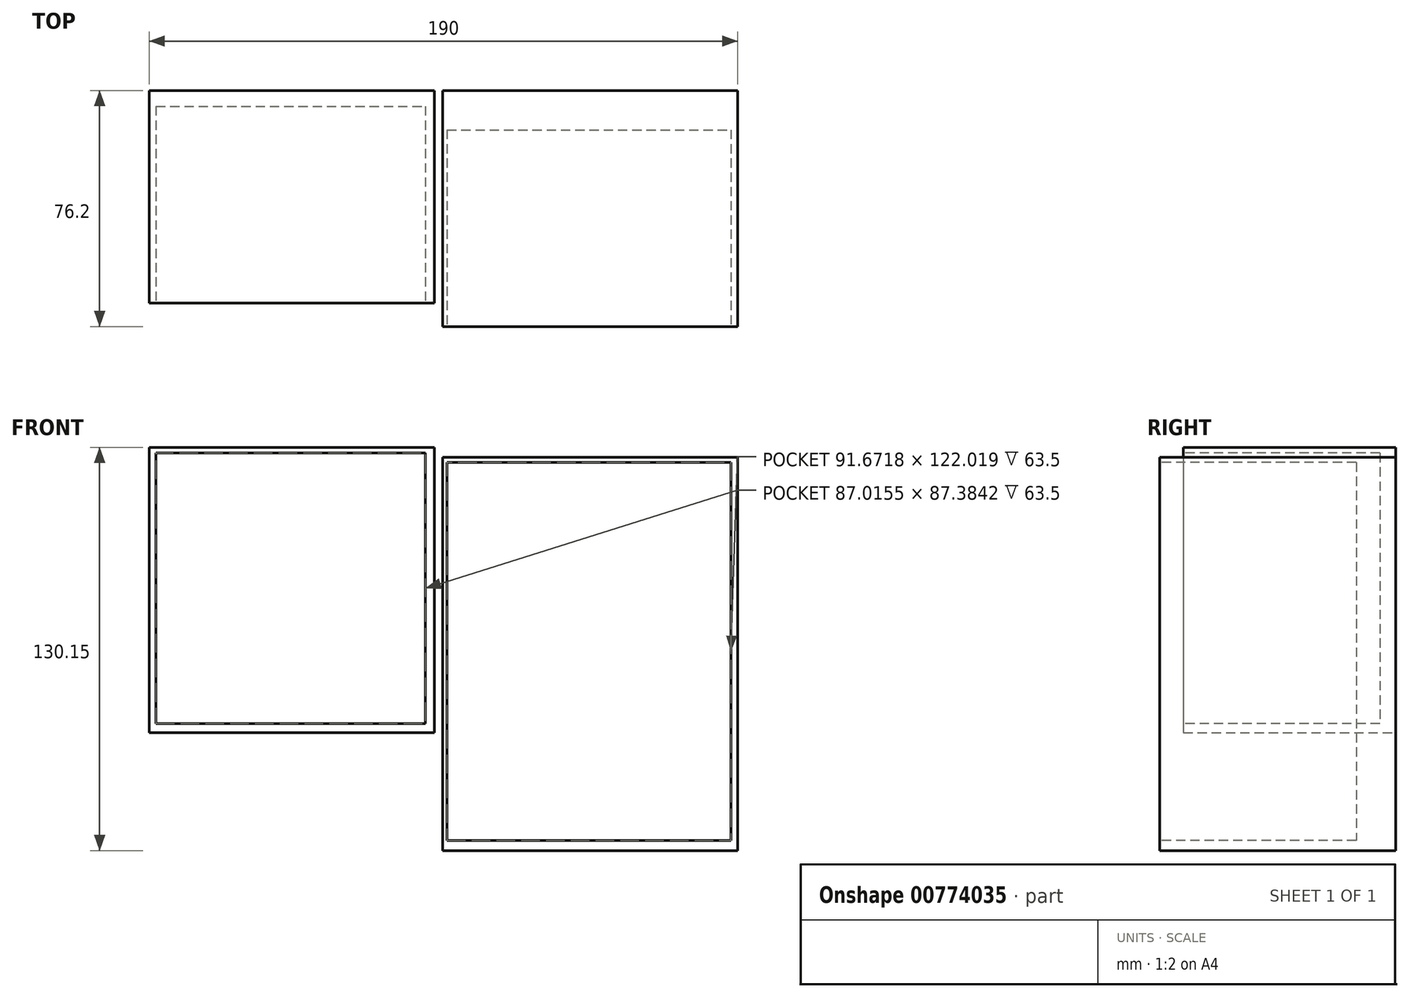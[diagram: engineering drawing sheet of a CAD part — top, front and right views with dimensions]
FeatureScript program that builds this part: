
annotation { "Feature Type Name" : "Feature", "Feature Type Description" : "" }
export const myFeature = defineFeature(function(context is Context, id is Id, definition is map)
    precondition{}
    {
        {
            var Q0;
            Q0=qCreatedBy(makeId("Front.planeOp"),FACE);
            var sketch = newSketch(context, id + "F0", { "sketchPlane" : qUnion([Q0])});
            skLineSegment(sketch, "E0.bottom", {"start": v(-81.71, 66.08) * mm, "end": v(10.36, 66.08) * mm});
            skLineSegment(sketch, "E0.top", {"start": v(-81.71, -26) * mm, "end": v(10.36, -26) * mm});
            skLineSegment(sketch, "E0.left", {"start": v(-81.71, 66.08) * mm, "end": v(-81.71, -26) * mm});
            skLineSegment(sketch, "E0.right", {"start": v(10.36, 66.08) * mm, "end": v(10.36, -26) * mm});
            skSolve(sketch);
        }
        {
            var Q0;
            Q0=makeQuery(id+"F0.imprint","IMPRINT",FACE,{"disambiguationData":[TD([[makeQuery(id+"F0.imprint","IMPRINT",EDGE,{"derivedFrom":sQuery(id+"F0.wireOp",EDGE,"E0.bottom")}),-1.0]])]});
            extrude(context, id + "F1", {"entities" : qUnion([Q0]), "depth" : 68.58 * mm, "offsetDistance" : 25.4 * mm});
        }
        {
            var Q0;
            Q0=makeQuery(id+"F1.opExtrude","CAP_FACE",FACE,{"disambiguationData":[OSD([sQuery(id+"F0.wireOp",EDGE,"E0.bottom"),sQuery(id+"F0.wireOp",EDGE,"E0.top"),sQuery(id+"F0.wireOp",EDGE,"E0.left"),sQuery(id+"F0.wireOp",EDGE,"E0.right")])],"isStart":false});
            var sketch = newSketch(context, id + "F2", { "sketchPlane" : qUnion([Q0])});
            skLineSegment(sketch, "E1.bottom", {"start": v(-79.54, 64.25) * mm, "end": v(7.48, 64.25) * mm});
            skLineSegment(sketch, "E1.top", {"start": v(-79.54, -23.14) * mm, "end": v(7.48, -23.14) * mm});
            skLineSegment(sketch, "E1.left", {"start": v(-79.54, 64.25) * mm, "end": v(-79.54, -23.14) * mm});
            skLineSegment(sketch, "E1.right", {"start": v(7.48, 64.25) * mm, "end": v(7.48, -23.14) * mm});
            skSolve(sketch);
        }
        {
            var Q0;
            Q0=makeQuery(id+"F2.imprint","IMPRINT",FACE,{"disambiguationData":[TD([[makeQuery(id+"F2.imprint","IMPRINT",EDGE,{"derivedFrom":sQuery(id+"F2.wireOp",EDGE,"E1.bottom")}),-1.0]])]});
            extrude(context, id + "F3", {"entities" : qUnion([Q0]), "operationType" : NewBodyOperationType.REMOVE, "oppositeDirection" : true, "depth" : 63.5 * mm, "offsetDistance" : 25.4 * mm});
        }
        {
            var Q0;
            Q0=qCreatedBy(makeId("Front.planeOp"),FACE);
            var sketch = newSketch(context, id + "F4", { "sketchPlane" : qUnion([Q0])});
            skLineSegment(sketch, "E2.bottom", {"start": v(13.04, 62.93) * mm, "end": v(108.3, 62.93) * mm});
            skLineSegment(sketch, "E2.top", {"start": v(13.04, -64.07) * mm, "end": v(108.3, -64.07) * mm});
            skLineSegment(sketch, "E2.left", {"start": v(13.04, 62.93) * mm, "end": v(13.04, -64.07) * mm});
            skLineSegment(sketch, "E2.right", {"start": v(108.3, 62.93) * mm, "end": v(108.3, -64.07) * mm});
            skSolve(sketch);
        }
        {
            var Q0;
            Q0=makeQuery(id+"F4.imprint","IMPRINT",FACE,{"disambiguationData":[TD([[makeQuery(id+"F4.imprint","IMPRINT",EDGE,{"derivedFrom":sQuery(id+"F4.wireOp",EDGE,"E2.bottom")}),-1.0]])]});
            extrude(context, id + "F5", {"entities" : qUnion([Q0]), "depth" : 76.2 * mm, "offsetDistance" : 25.4 * mm});
        }
        {
            var Q0;
            Q0=makeQuery(id+"F5.opExtrude","CAP_FACE",FACE,{"disambiguationData":[OSD([sQuery(id+"F4.wireOp",EDGE,"E2.bottom"),sQuery(id+"F4.wireOp",EDGE,"E2.top"),sQuery(id+"F4.wireOp",EDGE,"E2.left"),sQuery(id+"F4.wireOp",EDGE,"E2.right")])],"isStart":false});
            var sketch = newSketch(context, id + "F6", { "sketchPlane" : qUnion([Q0])});
            skLineSegment(sketch, "E3.bottom", {"start": v(14.44, 61.24) * mm, "end": v(106.11, 61.24) * mm});
            skLineSegment(sketch, "E3.top", {"start": v(14.44, -60.78) * mm, "end": v(106.11, -60.78) * mm});
            skLineSegment(sketch, "E3.left", {"start": v(14.44, 61.24) * mm, "end": v(14.44, -60.78) * mm});
            skLineSegment(sketch, "E3.right", {"start": v(106.11, 61.24) * mm, "end": v(106.11, -60.78) * mm});
            skSolve(sketch);
        }
        {
            var Q0;
            Q0=makeQuery(id+"F6.imprint","IMPRINT",FACE,{"disambiguationData":[TD([[makeQuery(id+"F6.imprint","IMPRINT",EDGE,{"derivedFrom":sQuery(id+"F6.wireOp",EDGE,"E3.bottom")}),-1.0]])]});
            extrude(context, id + "F7", {"entities" : qUnion([Q0]), "operationType" : NewBodyOperationType.REMOVE, "oppositeDirection" : true, "depth" : 63.5 * mm, "offsetDistance" : 25.4 * mm});
        }
    });
